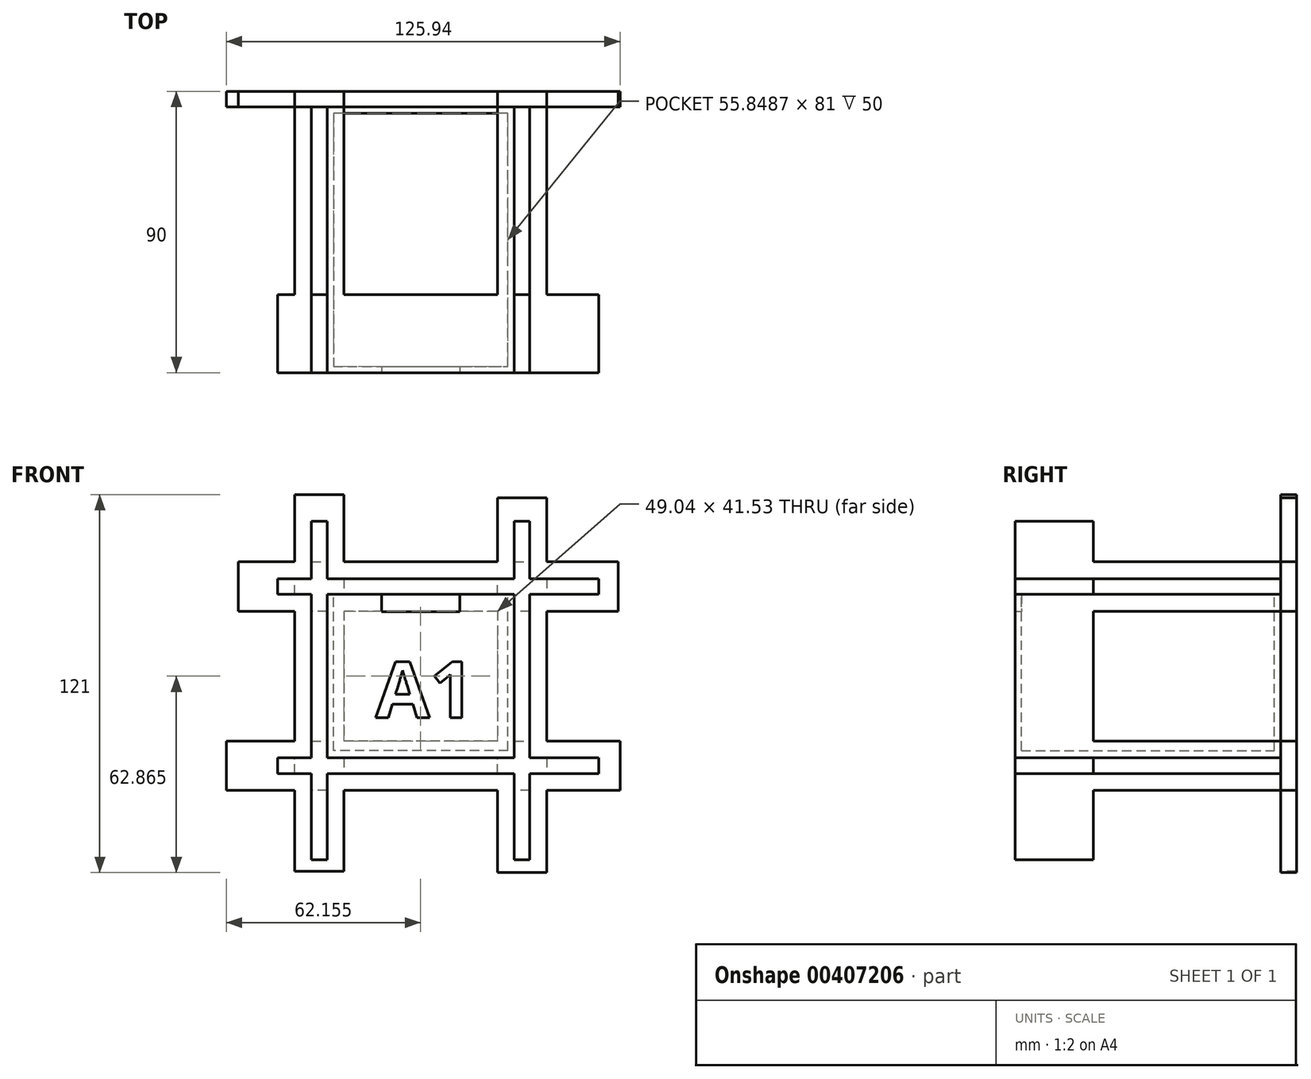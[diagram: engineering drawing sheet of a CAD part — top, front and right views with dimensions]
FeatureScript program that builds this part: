
annotation { "Feature Type Name" : "Feature", "Feature Type Description" : "" }
export const myFeature = defineFeature(function(context is Context, id is Id, definition is map)
    precondition{}
    {
        {
            var Q0;
            Q0=qCreatedBy(makeId("Front.planeOp"),FACE);
            var sketch = newSketch(context, id + "F0", { "sketchPlane" : qUnion([Q0])});
            skLineSegment(sketch, "E0", {"start": v(-42.77, 35.45) * mm, "end": v(59.87, 35.45) * mm});
            skLineSegment(sketch, "E1", {"start": v(-42.77, -21.88) * mm, "end": v(59.87, -21.88) * mm});
            skLineSegment(sketch, "E2", {"start": v(-26.96, 53.87) * mm, "end": v(-26.96, -54.47) * mm});
            skLineSegment(sketch, "E3", {"start": v(37.89, 53.87) * mm, "end": v(37.89, -54.47) * mm});
            skLineSegment(sketch, "E4.0", {"start": v(-31.96, 53.87) * mm, "end": v(-31.96, -54.47) * mm});
            skLineSegment(sketch, "E5.0", {"start": v(-42.77, 30.45) * mm, "end": v(59.87, 30.45) * mm});
            skLineSegment(sketch, "E6.0", {"start": v(32.89, 53.87) * mm, "end": v(32.89, -54.47) * mm});
            skLineSegment(sketch, "E7.0", {"start": v(-42.77, -26.88) * mm, "end": v(59.87, -26.88) * mm});
            skPoint(sketch, "E8", {"position": v(-31.96, 35.45) * mm});
            skPoint(sketch, "E9", {"position": v(-26.96, 35.45) * mm});
            skPoint(sketch, "E10", {"position": v(-26.96, 30.45) * mm});
            skPoint(sketch, "E11", {"position": v(-31.96, 30.45) * mm});
            skPoint(sketch, "E12", {"position": v(32.89, 35.45) * mm});
            skPoint(sketch, "E13", {"position": v(37.89, 35.45) * mm});
            skPoint(sketch, "E14", {"position": v(37.89, 30.45) * mm});
            skPoint(sketch, "E15", {"position": v(32.89, 30.45) * mm});
            skPoint(sketch, "E16", {"position": v(-26.96, -21.88) * mm});
            skPoint(sketch, "E17", {"position": v(32.89, -21.88) * mm});
            skPoint(sketch, "E18", {"position": v(37.89, -21.88) * mm});
            skPoint(sketch, "E19", {"position": v(32.89, -26.88) * mm});
            skPoint(sketch, "E20", {"position": v(37.89, -26.88) * mm});
            skPoint(sketch, "E21", {"position": v(-31.96, -26.88) * mm});
            skPoint(sketch, "E22", {"position": v(-31.96, -21.88) * mm});
            skPoint(sketch, "E23", {"position": v(-26.96, -26.88) * mm});
            skLineSegment(sketch, "E24", {"start": v(-31.96, 53.87) * mm, "end": v(-26.96, 53.87) * mm});
            skLineSegment(sketch, "E25", {"start": v(32.89, 53.87) * mm, "end": v(37.89, 53.87) * mm});
            skLineSegment(sketch, "E26", {"start": v(59.87, 35.45) * mm, "end": v(59.87, 30.45) * mm});
            skLineSegment(sketch, "E27", {"start": v(59.87, -21.88) * mm, "end": v(59.87, -26.88) * mm});
            skLineSegment(sketch, "E28", {"start": v(-42.77, -26.88) * mm, "end": v(-42.77, -21.88) * mm});
            skLineSegment(sketch, "E29", {"start": v(-31.96, -54.47) * mm, "end": v(-26.96, -54.47) * mm});
            skLineSegment(sketch, "E30", {"start": v(32.89, -54.47) * mm, "end": v(37.89, -54.47) * mm});
            skLineSegment(sketch, "E31", {"start": v(-42.77, 35.45) * mm, "end": v(-42.77, 30.45) * mm});
            skSolve(sketch);
        }
        {
            var Q0;
            {var subQ0=sQuery(id+"F0.wireOp",EDGE,"E2");var subQ1=sQuery(id+"F0.wireOp",EDGE,"E0");var subQ2=makeQuery(id+"F0.imprint","INTERSECT",VERTEX,{"derivedFrom":[subQ1,subQ0]});Q0=makeQuery(id+"F0.imprint","IMPRINT",FACE,{"disambiguationData":[TD([[makeQuery(id+"F0.imprint","IMPRINT",EDGE,{"disambiguationData":[TD([[subQ2,-1.0]])],"derivedFrom":subQ1}),-1.0]])]});}
            var Q1;
            {var subQ0=sQuery(id+"F0.wireOp",EDGE,"E3");var subQ1=sQuery(id+"F0.wireOp",EDGE,"E0");var subQ2=makeQuery(id+"F0.imprint","INTERSECT",VERTEX,{"derivedFrom":[subQ1,subQ0]});Q1=makeQuery(id+"F0.imprint","IMPRINT",FACE,{"disambiguationData":[TD([[makeQuery(id+"F0.imprint","IMPRINT",EDGE,{"disambiguationData":[TD([[subQ2,1.0]])],"derivedFrom":subQ1}),-1.0]])]});}
            var Q2;
            {var subQ0=sQuery(id+"F0.wireOp",EDGE,"E3");var subQ1=sQuery(id+"F0.wireOp",EDGE,"E1");var subQ2=makeQuery(id+"F0.imprint","INTERSECT",VERTEX,{"derivedFrom":[subQ1,subQ0]});Q2=makeQuery(id+"F0.imprint","IMPRINT",FACE,{"disambiguationData":[TD([[makeQuery(id+"F0.imprint","IMPRINT",EDGE,{"disambiguationData":[TD([[subQ2,1.0]])],"derivedFrom":subQ1}),1.0]])]});}
            var Q3;
            {var subQ0=sQuery(id+"F0.wireOp",EDGE,"E4.0");var subQ1=sQuery(id+"F0.wireOp",EDGE,"E0");var subQ2=makeQuery(id+"F0.imprint","INTERSECT",VERTEX,{"derivedFrom":[subQ1,subQ0]});Q3=makeQuery(id+"F0.imprint","IMPRINT",FACE,{"disambiguationData":[TD([[makeQuery(id+"F0.imprint","IMPRINT",EDGE,{"disambiguationData":[TD([[subQ2,-1.0]])],"derivedFrom":subQ1}),-1.0]])]});}
            var Q4;
            {var subQ0=sQuery(id+"F0.wireOp",EDGE,"E4.0");var subQ1=sQuery(id+"F0.wireOp",EDGE,"E1");var subQ2=makeQuery(id+"F0.imprint","INTERSECT",VERTEX,{"derivedFrom":[subQ1,subQ0]});Q4=makeQuery(id+"F0.imprint","IMPRINT",FACE,{"disambiguationData":[TD([[makeQuery(id+"F0.imprint","IMPRINT",EDGE,{"disambiguationData":[TD([[subQ2,-1.0]])],"derivedFrom":subQ1}),1.0]])]});}
            var Q5;
            {var subQ0=sQuery(id+"F0.wireOp",EDGE,"E4.0");var subQ1=sQuery(id+"F0.wireOp",EDGE,"E1");var subQ2=makeQuery(id+"F0.imprint","INTERSECT",VERTEX,{"derivedFrom":[subQ1,subQ0]});Q5=makeQuery(id+"F0.imprint","IMPRINT",FACE,{"disambiguationData":[TD([[makeQuery(id+"F0.imprint","IMPRINT",EDGE,{"disambiguationData":[TD([[subQ2,-1.0]])],"derivedFrom":subQ1}),-1.0]])]});}
            var Q6;
            {var subQ0=sQuery(id+"F0.wireOp",EDGE,"E2");var subQ1=sQuery(id+"F0.wireOp",EDGE,"E1");var subQ2=makeQuery(id+"F0.imprint","INTERSECT",VERTEX,{"derivedFrom":[subQ1,subQ0]});Q6=makeQuery(id+"F0.imprint","IMPRINT",FACE,{"disambiguationData":[TD([[makeQuery(id+"F0.imprint","IMPRINT",EDGE,{"disambiguationData":[TD([[subQ2,-1.0]])],"derivedFrom":subQ1}),-1.0]])]});}
            var Q7;
            {var subQ0=sQuery(id+"F0.wireOp",EDGE,"E3");var subQ1=sQuery(id+"F0.wireOp",EDGE,"E1");var subQ2=makeQuery(id+"F0.imprint","INTERSECT",VERTEX,{"derivedFrom":[subQ1,subQ0]});Q7=makeQuery(id+"F0.imprint","IMPRINT",FACE,{"disambiguationData":[TD([[makeQuery(id+"F0.imprint","IMPRINT",EDGE,{"disambiguationData":[TD([[subQ2,1.0]])],"derivedFrom":subQ1}),-1.0]])]});}
            var Q8;
            {var subQ0=sQuery(id+"F0.wireOp",EDGE,"E26");Q8=makeQuery(id+"F0.imprint","IMPRINT",FACE,{"disambiguationData":[TD([[makeQuery(id+"F0.imprint","IMPRINT",EDGE,{"derivedFrom":subQ0}),-1.0]])]});}
            var Q9;
            {var subQ5=sQuery(id+"F0.wireOp",EDGE,"E25");Q9=makeQuery(id+"F0.imprint","IMPRINT",FACE,{"disambiguationData":[TD([[makeQuery(id+"F0.imprint","IMPRINT",EDGE,{"derivedFrom":subQ5}),-1.0]])]});}
            var Q10;
            {var subQ0=sQuery(id+"F0.wireOp",EDGE,"E27");Q10=makeQuery(id+"F0.imprint","IMPRINT",FACE,{"disambiguationData":[TD([[makeQuery(id+"F0.imprint","IMPRINT",EDGE,{"derivedFrom":subQ0}),-1.0]])]});}
            var Q11;
            {var subQ0=sQuery(id+"F0.wireOp",EDGE,"E30");Q11=makeQuery(id+"F0.imprint","IMPRINT",FACE,{"disambiguationData":[TD([[makeQuery(id+"F0.imprint","IMPRINT",EDGE,{"derivedFrom":subQ0}),1.0]])]});}
            var Q12;
            {var subQ0=sQuery(id+"F0.wireOp",EDGE,"E29");Q12=makeQuery(id+"F0.imprint","IMPRINT",FACE,{"disambiguationData":[TD([[makeQuery(id+"F0.imprint","IMPRINT",EDGE,{"derivedFrom":subQ0}),1.0]])]});}
            var Q13;
            {var subQ0=sQuery(id+"F0.wireOp",EDGE,"E28");Q13=makeQuery(id+"F0.imprint","IMPRINT",FACE,{"disambiguationData":[TD([[makeQuery(id+"F0.imprint","IMPRINT",EDGE,{"derivedFrom":subQ0}),-1.0]])]});}
            var Q14;
            {var subQ0=sQuery(id+"F0.wireOp",EDGE,"E31");Q14=makeQuery(id+"F0.imprint","IMPRINT",FACE,{"disambiguationData":[TD([[makeQuery(id+"F0.imprint","IMPRINT",EDGE,{"derivedFrom":subQ0}),1.0]])]});}
            var Q15;
            {var subQ5=sQuery(id+"F0.wireOp",EDGE,"E24");Q15=makeQuery(id+"F0.imprint","IMPRINT",FACE,{"disambiguationData":[TD([[makeQuery(id+"F0.imprint","IMPRINT",EDGE,{"derivedFrom":subQ5}),-1.0]])]});}
            extrude(context, id + "F1", {"entities" : qUnion([Q0, Q1, Q2, Q3, Q4, Q5, Q6, Q7, Q8, Q9, Q10, Q11, Q12, Q13, Q14, Q15]), "depth" : 25 * mm});
        }
        {
            var Q0;
            Q0=makeQuery(id+"F1.opExtrude","CAP_FACE",FACE,{"disambiguationData":[OSD([sQuery(id+"F0.wireOp",EDGE,"E0"),sQuery(id+"F0.wireOp",EDGE,"E1"),sQuery(id+"F0.wireOp",EDGE,"E2"),sQuery(id+"F0.wireOp",EDGE,"E3"),sQuery(id+"F0.wireOp",EDGE,"E4.0"),sQuery(id+"F0.wireOp",EDGE,"E5.0"),sQuery(id+"F0.wireOp",EDGE,"E6.0"),sQuery(id+"F0.wireOp",EDGE,"E7.0"),sQuery(id+"F0.wireOp",EDGE,"E24"),sQuery(id+"F0.wireOp",EDGE,"E25"),sQuery(id+"F0.wireOp",EDGE,"E26"),sQuery(id+"F0.wireOp",EDGE,"E27"),sQuery(id+"F0.wireOp",EDGE,"E28"),sQuery(id+"F0.wireOp",EDGE,"E29"),sQuery(id+"F0.wireOp",EDGE,"E30"),sQuery(id+"F0.wireOp",EDGE,"E31")])],"isStart":true});
            var sketch = newSketch(context, id + "F2", { "sketchPlane" : qUnion([Q0])});
            skLineSegment(sketch, "E32", {"start": v(-37.89, 40.86) * mm, "end": v(-37.89, 35.45) * mm});
            skLineSegment(sketch, "E33", {"start": v(-37.89, 35.45) * mm, "end": v(-43.3, 35.45) * mm});
            skLineSegment(sketch, "E34", {"start": v(-43.3, 35.45) * mm, "end": v(-43.3, 30.45) * mm});
            skLineSegment(sketch, "E35", {"start": v(-43.3, 30.45) * mm, "end": v(-37.89, 30.45) * mm});
            skLineSegment(sketch, "E36", {"start": v(-37.89, 30.45) * mm, "end": v(-37.89, 25.05) * mm});
            skLineSegment(sketch, "E37", {"start": v(-37.89, 25.05) * mm, "end": v(-32.89, 25.05) * mm});
            skLineSegment(sketch, "E38", {"start": v(-32.89, 25.05) * mm, "end": v(-32.89, 30.45) * mm});
            skLineSegment(sketch, "E39", {"start": v(-32.89, 30.45) * mm, "end": v(-27.49, 30.45) * mm});
            skLineSegment(sketch, "E40", {"start": v(-27.49, 30.45) * mm, "end": v(-27.49, 35.45) * mm});
            skLineSegment(sketch, "E41", {"start": v(-27.49, 35.45) * mm, "end": v(-32.89, 35.45) * mm});
            skLineSegment(sketch, "E42", {"start": v(-32.89, 35.45) * mm, "end": v(-32.89, 40.86) * mm});
            skLineSegment(sketch, "E43", {"start": v(-32.89, 40.86) * mm, "end": v(-37.89, 40.86) * mm});
            skLineSegment(sketch, "E44", {"start": v(26.96, 40.86) * mm, "end": v(26.96, 35.45) * mm});
            skLineSegment(sketch, "E45", {"start": v(26.96, 35.45) * mm, "end": v(21.56, 35.45) * mm});
            skLineSegment(sketch, "E46", {"start": v(21.56, 35.45) * mm, "end": v(21.56, 30.45) * mm});
            skLineSegment(sketch, "E47", {"start": v(21.56, 30.45) * mm, "end": v(26.96, 30.45) * mm});
            skLineSegment(sketch, "E48", {"start": v(26.96, 30.45) * mm, "end": v(26.96, 25.05) * mm});
            skLineSegment(sketch, "E49", {"start": v(26.96, 25.05) * mm, "end": v(31.96, 25.05) * mm});
            skLineSegment(sketch, "E50", {"start": v(31.96, 25.05) * mm, "end": v(31.96, 30.45) * mm});
            skLineSegment(sketch, "E51", {"start": v(31.96, 30.45) * mm, "end": v(37.36, 30.45) * mm});
            skLineSegment(sketch, "E52", {"start": v(37.36, 30.45) * mm, "end": v(37.36, 35.45) * mm});
            skLineSegment(sketch, "E53", {"start": v(37.36, 35.45) * mm, "end": v(31.96, 35.45) * mm});
            skLineSegment(sketch, "E54", {"start": v(31.96, 35.45) * mm, "end": v(31.96, 40.86) * mm});
            skLineSegment(sketch, "E55", {"start": v(31.96, 40.86) * mm, "end": v(26.96, 40.86) * mm});
            skLineSegment(sketch, "E56", {"start": v(-37.89, -16.48) * mm, "end": v(-37.89, -21.88) * mm});
            skLineSegment(sketch, "E57", {"start": v(-37.89, -21.88) * mm, "end": v(-43.3, -21.88) * mm});
            skLineSegment(sketch, "E58", {"start": v(-43.3, -21.88) * mm, "end": v(-43.3, -26.88) * mm});
            skLineSegment(sketch, "E59", {"start": v(-43.3, -26.88) * mm, "end": v(-37.89, -26.88) * mm});
            skLineSegment(sketch, "E60", {"start": v(-37.89, -26.88) * mm, "end": v(-37.89, -32.29) * mm});
            skLineSegment(sketch, "E61", {"start": v(-37.89, -32.29) * mm, "end": v(-32.89, -32.29) * mm});
            skLineSegment(sketch, "E62", {"start": v(-32.89, -32.29) * mm, "end": v(-32.89, -26.88) * mm});
            skLineSegment(sketch, "E63", {"start": v(-32.89, -26.88) * mm, "end": v(-27.49, -26.88) * mm});
            skLineSegment(sketch, "E64", {"start": v(-27.49, -26.88) * mm, "end": v(-27.49, -21.88) * mm});
            skLineSegment(sketch, "E65", {"start": v(-27.49, -21.88) * mm, "end": v(-32.89, -21.88) * mm});
            skLineSegment(sketch, "E66", {"start": v(-32.89, -21.88) * mm, "end": v(-32.89, -16.48) * mm});
            skLineSegment(sketch, "E67", {"start": v(-32.89, -16.48) * mm, "end": v(-37.89, -16.48) * mm});
            skLineSegment(sketch, "E68", {"start": v(26.96, -16.48) * mm, "end": v(26.96, -21.88) * mm});
            skLineSegment(sketch, "E69", {"start": v(26.96, -21.88) * mm, "end": v(21.56, -21.88) * mm});
            skLineSegment(sketch, "E70", {"start": v(21.56, -21.88) * mm, "end": v(21.56, -26.88) * mm});
            skLineSegment(sketch, "E71", {"start": v(21.56, -26.88) * mm, "end": v(26.96, -26.88) * mm});
            skLineSegment(sketch, "E72", {"start": v(26.96, -26.88) * mm, "end": v(26.96, -32.29) * mm});
            skLineSegment(sketch, "E73", {"start": v(26.96, -32.29) * mm, "end": v(31.96, -32.29) * mm});
            skLineSegment(sketch, "E74", {"start": v(31.96, -32.29) * mm, "end": v(31.96, -26.88) * mm});
            skLineSegment(sketch, "E75", {"start": v(31.96, -26.88) * mm, "end": v(37.36, -26.88) * mm});
            skLineSegment(sketch, "E76", {"start": v(37.36, -26.88) * mm, "end": v(37.36, -21.88) * mm});
            skLineSegment(sketch, "E77", {"start": v(37.36, -21.88) * mm, "end": v(31.96, -21.88) * mm});
            skLineSegment(sketch, "E78", {"start": v(31.96, -21.88) * mm, "end": v(31.96, -16.48) * mm});
            skLineSegment(sketch, "E79", {"start": v(31.96, -16.48) * mm, "end": v(26.96, -16.48) * mm});
            skSolve(sketch);
        }
        {
            var Q0;
            Q0=makeQuery(id+"F2.imprint","IMPRINT",FACE,{"disambiguationData":[TD([[makeQuery(id+"F2.imprint","IMPRINT",EDGE,{"derivedFrom":sQuery(id+"F2.wireOp",EDGE,"E32")}),1.0]])]});
            var Q1;
            Q1=makeQuery(id+"F2.imprint","IMPRINT",FACE,{"disambiguationData":[TD([[makeQuery(id+"F2.imprint","IMPRINT",EDGE,{"derivedFrom":sQuery(id+"F2.wireOp",EDGE,"E44")}),1.0]])]});
            var Q2;
            Q2=makeQuery(id+"F2.imprint","IMPRINT",FACE,{"disambiguationData":[TD([[makeQuery(id+"F2.imprint","IMPRINT",EDGE,{"derivedFrom":sQuery(id+"F2.wireOp",EDGE,"E68")}),1.0]])]});
            var Q3;
            Q3=makeQuery(id+"F2.imprint","IMPRINT",FACE,{"disambiguationData":[TD([[makeQuery(id+"F2.imprint","IMPRINT",EDGE,{"derivedFrom":sQuery(id+"F2.wireOp",EDGE,"E56")}),1.0]])]});
            extrude(context, id + "F3", {"entities" : qUnion([Q0, Q1, Q2, Q3]), "operationType" : NewBodyOperationType.ADD, "depth" : 60 * mm});
        }
        {
            var Q0;
            Q0=makeQuery(id+"F3.opExtrude","CAP_FACE",FACE,{"disambiguationData":[OSD([sQuery(id+"F2.wireOp",EDGE,"E32"),sQuery(id+"F2.wireOp",EDGE,"E33"),sQuery(id+"F2.wireOp",EDGE,"E34"),sQuery(id+"F2.wireOp",EDGE,"E35"),sQuery(id+"F2.wireOp",EDGE,"E36"),sQuery(id+"F2.wireOp",EDGE,"E37"),sQuery(id+"F2.wireOp",EDGE,"E38"),sQuery(id+"F2.wireOp",EDGE,"E39"),sQuery(id+"F2.wireOp",EDGE,"E40"),sQuery(id+"F2.wireOp",EDGE,"E41"),sQuery(id+"F2.wireOp",EDGE,"E42"),sQuery(id+"F2.wireOp",EDGE,"E43")])],"isStart":false});
            var sketch = newSketch(context, id + "F4", { "sketchPlane" : qUnion([Q0])});
            skLineSegment(sketch, "E80.bottom", {"start": v(-43.3, 40.86) * mm, "end": v(-27.49, 40.86) * mm});
            skLineSegment(sketch, "E80.top", {"start": v(-43.3, 25.05) * mm, "end": v(-27.49, 25.05) * mm});
            skLineSegment(sketch, "E80.left", {"start": v(-43.3, 40.86) * mm, "end": v(-43.3, 25.05) * mm});
            skLineSegment(sketch, "E80.right", {"start": v(-27.49, 40.86) * mm, "end": v(-27.49, 25.05) * mm});
            skLineSegment(sketch, "E81.bottom", {"start": v(21.56, 40.86) * mm, "end": v(37.36, 40.86) * mm});
            skLineSegment(sketch, "E81.top", {"start": v(21.56, 25.05) * mm, "end": v(37.36, 25.05) * mm});
            skLineSegment(sketch, "E81.left", {"start": v(21.56, 40.86) * mm, "end": v(21.56, 25.05) * mm});
            skLineSegment(sketch, "E81.right", {"start": v(37.36, 40.86) * mm, "end": v(37.36, 25.05) * mm});
            skLineSegment(sketch, "E82.bottom", {"start": v(21.56, -16.48) * mm, "end": v(37.36, -16.48) * mm});
            skLineSegment(sketch, "E82.top", {"start": v(21.56, -32.29) * mm, "end": v(37.36, -32.29) * mm});
            skLineSegment(sketch, "E82.left", {"start": v(21.56, -16.48) * mm, "end": v(21.56, -32.29) * mm});
            skLineSegment(sketch, "E82.right", {"start": v(37.36, -16.48) * mm, "end": v(37.36, -32.29) * mm});
            skLineSegment(sketch, "E83.bottom", {"start": v(-43.3, -16.48) * mm, "end": v(-27.49, -16.48) * mm});
            skLineSegment(sketch, "E83.top", {"start": v(-43.3, -32.29) * mm, "end": v(-27.49, -32.29) * mm});
            skLineSegment(sketch, "E83.left", {"start": v(-43.3, -16.48) * mm, "end": v(-43.3, -32.29) * mm});
            skLineSegment(sketch, "E83.right", {"start": v(-27.49, -16.48) * mm, "end": v(-27.49, -32.29) * mm});
            skLineSegment(sketch, "E84", {"start": v(-27.49, -16.48) * mm, "end": v(21.56, -16.48) * mm});
            skLineSegment(sketch, "E85", {"start": v(21.56, -32.29) * mm, "end": v(-27.49, -32.29) * mm});
            skLineSegment(sketch, "E86", {"start": v(-27.49, 25.05) * mm, "end": v(-27.49, -16.48) * mm});
            skLineSegment(sketch, "E87", {"start": v(-43.3, -16.48) * mm, "end": v(-43.3, 25.05) * mm});
            skLineSegment(sketch, "E88", {"start": v(-27.49, 25.05) * mm, "end": v(21.56, 25.05) * mm});
            skLineSegment(sketch, "E89", {"start": v(21.56, 40.86) * mm, "end": v(-27.49, 40.86) * mm});
            skLineSegment(sketch, "E90", {"start": v(21.56, 25.05) * mm, "end": v(21.56, -16.48) * mm});
            skLineSegment(sketch, "E91", {"start": v(37.36, -16.48) * mm, "end": v(37.36, 25.05) * mm});
            skLineSegment(sketch, "E92.bottom", {"start": v(-43.3, 40.86) * mm, "end": v(-66.14, 40.86) * mm});
            skLineSegment(sketch, "E92.top", {"start": v(-43.3, 25.05) * mm, "end": v(-66.14, 25.05) * mm});
            skLineSegment(sketch, "E92.right", {"start": v(-66.14, 40.86) * mm, "end": v(-66.14, 25.05) * mm});
            skLineSegment(sketch, "E93.top", {"start": v(-43.3, 61.3) * mm, "end": v(-27.49, 61.3) * mm});
            skLineSegment(sketch, "E93.left", {"start": v(-43.3, 40.86) * mm, "end": v(-43.3, 61.3) * mm});
            skLineSegment(sketch, "E93.right", {"start": v(-27.49, 40.86) * mm, "end": v(-27.49, 61.3) * mm});
            skLineSegment(sketch, "E94.top", {"start": v(21.56, 62.42) * mm, "end": v(37.36, 62.42) * mm});
            skLineSegment(sketch, "E94.left", {"start": v(21.56, 40.86) * mm, "end": v(21.56, 62.42) * mm});
            skLineSegment(sketch, "E94.right", {"start": v(37.36, 40.86) * mm, "end": v(37.36, 62.42) * mm});
            skLineSegment(sketch, "E95.bottom", {"start": v(37.36, 25.05) * mm, "end": v(55.45, 25.05) * mm});
            skLineSegment(sketch, "E95.top", {"start": v(37.36, 40.86) * mm, "end": v(55.45, 40.86) * mm});
            skLineSegment(sketch, "E95.left", {"start": v(37.36, 25.05) * mm, "end": v(37.36, 40.86) * mm});
            skLineSegment(sketch, "E95.right", {"start": v(55.45, 25.05) * mm, "end": v(55.45, 40.86) * mm});
            skLineSegment(sketch, "E96.bottom", {"start": v(37.36, -32.29) * mm, "end": v(59.19, -32.29) * mm});
            skLineSegment(sketch, "E96.top", {"start": v(37.36, -16.48) * mm, "end": v(59.19, -16.48) * mm});
            skLineSegment(sketch, "E96.left", {"start": v(37.36, -32.29) * mm, "end": v(37.36, -16.48) * mm});
            skLineSegment(sketch, "E96.right", {"start": v(59.19, -32.29) * mm, "end": v(59.19, -16.48) * mm});
            skLineSegment(sketch, "E97.bottom", {"start": v(-43.3, -32.29) * mm, "end": v(-66.75, -32.29) * mm});
            skLineSegment(sketch, "E97.top", {"start": v(-43.3, -16.48) * mm, "end": v(-66.75, -16.48) * mm});
            skLineSegment(sketch, "E97.left", {"start": v(-43.3, -32.29) * mm, "end": v(-43.3, -16.48) * mm});
            skLineSegment(sketch, "E97.right", {"start": v(-66.75, -32.29) * mm, "end": v(-66.75, -16.48) * mm});
            skLineSegment(sketch, "E98.top", {"start": v(-43.3, -58.58) * mm, "end": v(-27.49, -58.58) * mm});
            skLineSegment(sketch, "E98.left", {"start": v(-43.3, -32.29) * mm, "end": v(-43.3, -58.58) * mm});
            skLineSegment(sketch, "E98.right", {"start": v(-27.49, -32.29) * mm, "end": v(-27.49, -58.58) * mm});
            skLineSegment(sketch, "E99.top", {"start": v(21.56, -58.2) * mm, "end": v(37.36, -58.2) * mm});
            skLineSegment(sketch, "E99.left", {"start": v(21.56, -32.29) * mm, "end": v(21.56, -58.2) * mm});
            skLineSegment(sketch, "E99.right", {"start": v(37.36, -32.29) * mm, "end": v(37.36, -58.2) * mm});
            skSolve(sketch);
        }
        {
            var Q0;
            {var subQ1=makeQuery(id+"F3.opExtrude","CAP_EDGE",EDGE,{"disambiguationData":[OSD([sQuery(id+"F2.wireOp",EDGE,"E32")])],"isStart":false});Q0=makeQuery(id+"F4.imprint","IMPRINT",FACE,{"disambiguationData":[TD([[makeQuery(id+"F4.imprint","IMPRINT",EDGE,{"derivedFrom":subQ1}),-1.0]])]});}
            var Q1;
            {var subQ2=makeQuery(id+"F3.opExtrude","CAP_EDGE",EDGE,{"disambiguationData":[OSD([sQuery(id+"F2.wireOp",EDGE,"E32")])],"isStart":false});Q1=makeQuery(id+"F4.imprint","IMPRINT",FACE,{"disambiguationData":[TD([[makeQuery(id+"F4.imprint","IMPRINT",EDGE,{"derivedFrom":subQ2}),1.0]])]});}
            var Q2;
            {var subQ4=makeQuery(id+"F3.opExtrude","CAP_EDGE",EDGE,{"disambiguationData":[OSD([sQuery(id+"F2.wireOp",EDGE,"E41")])],"isStart":false});Q2=makeQuery(id+"F4.imprint","IMPRINT",FACE,{"disambiguationData":[TD([[makeQuery(id+"F4.imprint","IMPRINT",EDGE,{"derivedFrom":subQ4}),-1.0]])]});}
            var Q3;
            {var subQ1=makeQuery(id+"F3.opExtrude","CAP_EDGE",EDGE,{"disambiguationData":[OSD([sQuery(id+"F2.wireOp",EDGE,"E38")])],"isStart":false});Q3=makeQuery(id+"F4.imprint","IMPRINT",FACE,{"disambiguationData":[TD([[makeQuery(id+"F4.imprint","IMPRINT",EDGE,{"derivedFrom":subQ1}),1.0]])]});}
            var Q4;
            {var subQ4=makeQuery(id+"F3.opExtrude","CAP_EDGE",EDGE,{"disambiguationData":[OSD([sQuery(id+"F2.wireOp",EDGE,"E35")])],"isStart":false});Q4=makeQuery(id+"F4.imprint","IMPRINT",FACE,{"disambiguationData":[TD([[makeQuery(id+"F4.imprint","IMPRINT",EDGE,{"derivedFrom":subQ4}),1.0]])]});}
            var Q5;
            Q5=makeQuery(id+"F4.imprint","IMPRINT",FACE,{"disambiguationData":[TD([[makeQuery(id+"F4.imprint","IMPRINT",EDGE,{"derivedFrom":sQuery(id+"F4.wireOp",EDGE,"E81.bottom")}),-1.0]])]});
            var Q6;
            Q6=makeQuery(id+"F4.imprint","IMPRINT",FACE,{"disambiguationData":[TD([[makeQuery(id+"F4.imprint","IMPRINT",EDGE,{"derivedFrom":sQuery(id+"F4.wireOp",EDGE,"E82.bottom")}),-1.0]])]});
            var Q7;
            Q7=makeQuery(id+"F4.imprint","IMPRINT",FACE,{"disambiguationData":[TD([[makeQuery(id+"F4.imprint","IMPRINT",EDGE,{"derivedFrom":sQuery(id+"F4.wireOp",EDGE,"E83.bottom")}),-1.0]])]});
            var Q8;
            Q8=makeQuery(id+"F4.imprint","IMPRINT",FACE,{"disambiguationData":[TD([[makeQuery(id+"F4.imprint","IMPRINT",EDGE,{"derivedFrom":sQuery(id+"F4.wireOp",EDGE,"E82.left")}),-1.0]])]});
            var Q9;
            Q9=makeQuery(id+"F4.imprint","IMPRINT",FACE,{"disambiguationData":[TD([[makeQuery(id+"F4.imprint","IMPRINT",EDGE,{"derivedFrom":sQuery(id+"F4.wireOp",EDGE,"E81.top")}),-1.0]])]});
            var Q10;
            Q10=makeQuery(id+"F4.imprint","IMPRINT",FACE,{"disambiguationData":[TD([[makeQuery(id+"F4.imprint","IMPRINT",EDGE,{"derivedFrom":sQuery(id+"F4.wireOp",EDGE,"E83.bottom")}),1.0]])]});
            var Q11;
            Q11=makeQuery(id+"F4.imprint","IMPRINT",FACE,{"disambiguationData":[TD([[makeQuery(id+"F4.imprint","IMPRINT",EDGE,{"derivedFrom":sQuery(id+"F4.wireOp",EDGE,"E81.left")}),-1.0]])]});
            var Q12;
            {var subQ3=sQuery(id+"F4.wireOp",EDGE,"E92.bottom");Q12=makeQuery(id+"F4.imprint","IMPRINT",FACE,{"disambiguationData":[TD([[makeQuery(id+"F4.imprint","IMPRINT",EDGE,{"derivedFrom":subQ3}),1.0]])]});}
            var Q13;
            Q13=makeQuery(id+"F4.imprint","IMPRINT",FACE,{"disambiguationData":[TD([[makeQuery(id+"F4.imprint","IMPRINT",EDGE,{"derivedFrom":sQuery(id+"F4.wireOp",EDGE,"E97.bottom")}),-1.0]])]});
            var Q14;
            Q14=makeQuery(id+"F4.imprint","IMPRINT",FACE,{"disambiguationData":[TD([[makeQuery(id+"F4.imprint","IMPRINT",EDGE,{"derivedFrom":sQuery(id+"F4.wireOp",EDGE,"E83.top")}),-1.0]])]});
            var Q15;
            Q15=makeQuery(id+"F4.imprint","IMPRINT",FACE,{"disambiguationData":[TD([[makeQuery(id+"F4.imprint","IMPRINT",EDGE,{"derivedFrom":sQuery(id+"F4.wireOp",EDGE,"E82.top")}),-1.0]])]});
            var Q16;
            Q16=makeQuery(id+"F4.imprint","IMPRINT",FACE,{"disambiguationData":[TD([[makeQuery(id+"F4.imprint","IMPRINT",EDGE,{"derivedFrom":sQuery(id+"F4.wireOp",EDGE,"E96.bottom")}),1.0]])]});
            var Q17;
            Q17=makeQuery(id+"F4.imprint","IMPRINT",FACE,{"disambiguationData":[TD([[makeQuery(id+"F4.imprint","IMPRINT",EDGE,{"derivedFrom":sQuery(id+"F4.wireOp",EDGE,"E81.top")}),1.0]])]});
            var Q18;
            Q18=makeQuery(id+"F4.imprint","IMPRINT",FACE,{"disambiguationData":[TD([[makeQuery(id+"F4.imprint","IMPRINT",EDGE,{"derivedFrom":sQuery(id+"F4.wireOp",EDGE,"E81.bottom")}),1.0]])]});
            var Q19;
            Q19=makeQuery(id+"F4.imprint","IMPRINT",FACE,{"disambiguationData":[TD([[makeQuery(id+"F4.imprint","IMPRINT",EDGE,{"derivedFrom":sQuery(id+"F4.wireOp",EDGE,"E95.bottom")}),1.0]])]});
            var Q20;
            Q20=makeQuery(id+"F4.imprint","IMPRINT",FACE,{"disambiguationData":[TD([[makeQuery(id+"F4.imprint","IMPRINT",EDGE,{"derivedFrom":sQuery(id+"F4.wireOp",EDGE,"E93.top")}),-1.0]])]});
            extrude(context, id + "F5", {"entities" : qUnion([Q0, Q1, Q2, Q3, Q4, Q5, Q6, Q7, Q8, Q9, Q10, Q11, Q12, Q13, Q14, Q15, Q16, Q17, Q18, Q19, Q20]), "operationType" : NewBodyOperationType.ADD, "depth" : 5 * mm});
        }
        {
            var Q0;
            Q0=makeQuery(id+"F1.opExtrude","CAP_FACE",FACE,{"disambiguationData":[OSD([sQuery(id+"F0.wireOp",EDGE,"E0"),sQuery(id+"F0.wireOp",EDGE,"E1"),sQuery(id+"F0.wireOp",EDGE,"E2"),sQuery(id+"F0.wireOp",EDGE,"E3"),sQuery(id+"F0.wireOp",EDGE,"E4.0"),sQuery(id+"F0.wireOp",EDGE,"E5.0"),sQuery(id+"F0.wireOp",EDGE,"E6.0"),sQuery(id+"F0.wireOp",EDGE,"E7.0"),sQuery(id+"F0.wireOp",EDGE,"E24"),sQuery(id+"F0.wireOp",EDGE,"E25"),sQuery(id+"F0.wireOp",EDGE,"E26"),sQuery(id+"F0.wireOp",EDGE,"E27"),sQuery(id+"F0.wireOp",EDGE,"E28"),sQuery(id+"F0.wireOp",EDGE,"E29"),sQuery(id+"F0.wireOp",EDGE,"E30"),sQuery(id+"F0.wireOp",EDGE,"E31")])],"isStart":false});
            var sketch = newSketch(context, id + "F6", { "sketchPlane" : qUnion([Q0])});
            skLineSegment(sketch, "E100.bottom", {"start": v(-26.96, 30.45) * mm, "end": v(32.89, 30.45) * mm});
            skLineSegment(sketch, "E100.top", {"start": v(-26.96, -21.88) * mm, "end": v(32.89, -21.88) * mm});
            skLineSegment(sketch, "E100.left", {"start": v(-26.96, 30.45) * mm, "end": v(-26.96, -21.88) * mm});
            skLineSegment(sketch, "E100.right", {"start": v(32.89, 30.45) * mm, "end": v(32.89, -21.88) * mm});
            skSolve(sketch);
        }
        {
            var Q0;
            Q0=makeQuery(id+"F6.imprint","IMPRINT",FACE,{"disambiguationData":[TD([[makeQuery(id+"F6.imprint","IMPRINT",EDGE,{"derivedFrom":sQuery(id+"F6.wireOp",EDGE,"E100.bottom")}),-1.0]])]});
            var Q1;
            Q1=makeQuery(id+"F5.opExtrude","CAP_FACE",FACE,{"disambiguationData":[OSD([sQuery(id+"F4.wireOp",EDGE,"E84"),sQuery(id+"F4.wireOp",EDGE,"E85"),sQuery(id+"F4.wireOp",EDGE,"E86"),sQuery(id+"F4.wireOp",EDGE,"E87"),sQuery(id+"F4.wireOp",EDGE,"E88"),sQuery(id+"F4.wireOp",EDGE,"E89"),sQuery(id+"F4.wireOp",EDGE,"E90"),sQuery(id+"F4.wireOp",EDGE,"E91"),sQuery(id+"F4.wireOp",EDGE,"E92.bottom"),sQuery(id+"F4.wireOp",EDGE,"E92.top"),sQuery(id+"F4.wireOp",EDGE,"E92.right"),sQuery(id+"F4.wireOp",EDGE,"E93.top"),sQuery(id+"F4.wireOp",EDGE,"E93.left"),sQuery(id+"F4.wireOp",EDGE,"E93.right"),sQuery(id+"F4.wireOp",EDGE,"E94.top"),sQuery(id+"F4.wireOp",EDGE,"E94.left"),sQuery(id+"F4.wireOp",EDGE,"E94.right"),sQuery(id+"F4.wireOp",EDGE,"E95.bottom"),sQuery(id+"F4.wireOp",EDGE,"E95.top"),sQuery(id+"F4.wireOp",EDGE,"E95.right"),sQuery(id+"F4.wireOp",EDGE,"E96.bottom"),sQuery(id+"F4.wireOp",EDGE,"E96.top"),sQuery(id+"F4.wireOp",EDGE,"E96.right"),sQuery(id+"F4.wireOp",EDGE,"E97.bottom"),sQuery(id+"F4.wireOp",EDGE,"E97.top"),sQuery(id+"F4.wireOp",EDGE,"E97.right"),sQuery(id+"F4.wireOp",EDGE,"E98.top"),sQuery(id+"F4.wireOp",EDGE,"E98.left"),sQuery(id+"F4.wireOp",EDGE,"E98.right"),sQuery(id+"F4.wireOp",EDGE,"E99.top"),sQuery(id+"F4.wireOp",EDGE,"E99.left"),sQuery(id+"F4.wireOp",EDGE,"E99.right")])],"isStart":true});
            extrude(context, id + "F7", {"entities" : qUnion([Q0]), "endBound" : BoundingType.UP_TO_SURFACE, "oppositeDirection" : true, "endBoundEntityFace" : qUnion([Q1]), "depth" : 5 * mm});
        }
        {
            var Q0;
            Q0=makeQuery(id+"F7.opExtrude","SWEPT_FACE",FACE,{"disambiguationData":[OSD([sQuery(id+"F6.wireOp",EDGE,"E100.bottom")])]});
            var sketch = newSketch(context, id + "F8", { "sketchPlane" : qUnion([Q0])});
            skLineSegment(sketch, "E101.bottom", {"start": v(-26.96, 60) * mm, "end": v(32.89, 60) * mm});
            skLineSegment(sketch, "E101.top", {"start": v(-26.96, -25) * mm, "end": v(32.89, -25) * mm});
            skLineSegment(sketch, "E101.left", {"start": v(-26.96, 60) * mm, "end": v(-26.96, -25) * mm});
            skLineSegment(sketch, "E101.right", {"start": v(32.89, 60) * mm, "end": v(32.89, -25) * mm});
            skLineSegment(sketch, "E102.0", {"start": v(30.89, 58) * mm, "end": v(-24.96, 58) * mm});
            skLineSegment(sketch, "E102.1", {"start": v(30.89, -23) * mm, "end": v(30.89, 58) * mm});
            skLineSegment(sketch, "E102.2", {"start": v(-24.96, -23) * mm, "end": v(30.89, -23) * mm});
            skLineSegment(sketch, "E102.3", {"start": v(-24.96, 58) * mm, "end": v(-24.96, -23) * mm});
            skSolve(sketch);
        }
        {
            var Q0;
            Q0=makeQuery(id+"F8.imprint","IMPRINT",FACE,{"disambiguationData":[TD([[makeQuery(id+"F8.imprint","IMPRINT",EDGE,{"derivedFrom":sQuery(id+"F8.wireOp",EDGE,"E102.0")}),1.0]])]});
            extrude(context, id + "F9", {"entities" : qUnion([Q0]), "operationType" : NewBodyOperationType.REMOVE, "oppositeDirection" : true, "depth" : 50 * mm});
        }
        {
            var Q0;
            Q0=makeQuery(id+"F7.opExtrude","CAP_FACE",FACE,{"disambiguationData":[OSD([sQuery(id+"F6.wireOp",EDGE,"E100.bottom"),sQuery(id+"F6.wireOp",EDGE,"E100.top"),sQuery(id+"F6.wireOp",EDGE,"E100.left"),sQuery(id+"F6.wireOp",EDGE,"E100.right")])],"isStart":true});
            var sketch = newSketch(context, id + "F10", { "sketchPlane" : qUnion([Q0])});
            skLineSegment(sketch, "E103.bottom", {"start": v(15.53, 24.9) * mm, "end": v(-9.6, 24.9) * mm});
            skLineSegment(sketch, "E103.top", {"start": v(15.53, 36) * mm, "end": v(-9.6, 36) * mm});
            skLineSegment(sketch, "E103.left", {"start": v(15.53, 24.9) * mm, "end": v(15.53, 36) * mm});
            skLineSegment(sketch, "E103.right", {"start": v(-9.6, 24.9) * mm, "end": v(-9.6, 36) * mm});
            skPoint(sketch, "E103.middle", {"position": v(2.97, 30.45) * mm});
            skSolve(sketch);
        }
        {
            var Q0;
            {var subQ0=sQuery(id+"F10.wireOp",EDGE,"E103.bottom");Q0=makeQuery(id+"F10.imprint","IMPRINT",FACE,{"disambiguationData":[TD([[makeQuery(id+"F10.imprint","IMPRINT",EDGE,{"derivedFrom":subQ0}),-1.0]])]});}
            var Q1;
            Q1=makeQuery(id+"F9.boolean.opBoolean","COPY",FACE,{"derivedFrom":makeQuery(id+"F9.opExtrude","SWEPT_FACE",FACE,{"disambiguationData":[OSD([sQuery(id+"F8.wireOp",EDGE,"E102.2")])]})});
            extrude(context, id + "F11", {"entities" : qUnion([Q0]), "operationType" : NewBodyOperationType.REMOVE, "endBound" : BoundingType.UP_TO_SURFACE, "oppositeDirection" : true, "endBoundEntityFace" : qUnion([Q1]), "depth" : 25 * mm});
        }
        {
            var Q0;
            Q0=makeQuery(id+"F7.opExtrude","CAP_FACE",FACE,{"disambiguationData":[OSD([sQuery(id+"F6.wireOp",EDGE,"E100.bottom"),sQuery(id+"F6.wireOp",EDGE,"E100.top"),sQuery(id+"F6.wireOp",EDGE,"E100.left"),sQuery(id+"F6.wireOp",EDGE,"E100.right")])],"isStart":true});
            var sketch = newSketch(context, id + "F12", { "sketchPlane" : qUnion([Q0])});
            skText(sketch, "E104", { "text": "A1", "fontName": "OpenSans-Bold.ttf"});
            const initialGuessF12  = {"E104": [-0.01145, -0.00899, 1, 0, 0.01802]};
            skSetInitialGuess(sketch, initialGuessF12);
            skSolve(sketch);
        }
        {
            var Q0;
            Q0 = qSketchRegion(id + "F12", true);
            extrude(context, id + "F13", {"entities" : qUnion([Q0]), "operationType" : NewBodyOperationType.REMOVE, "oppositeDirection" : true, "depth" : 0.1 * mm});
        }
    });
